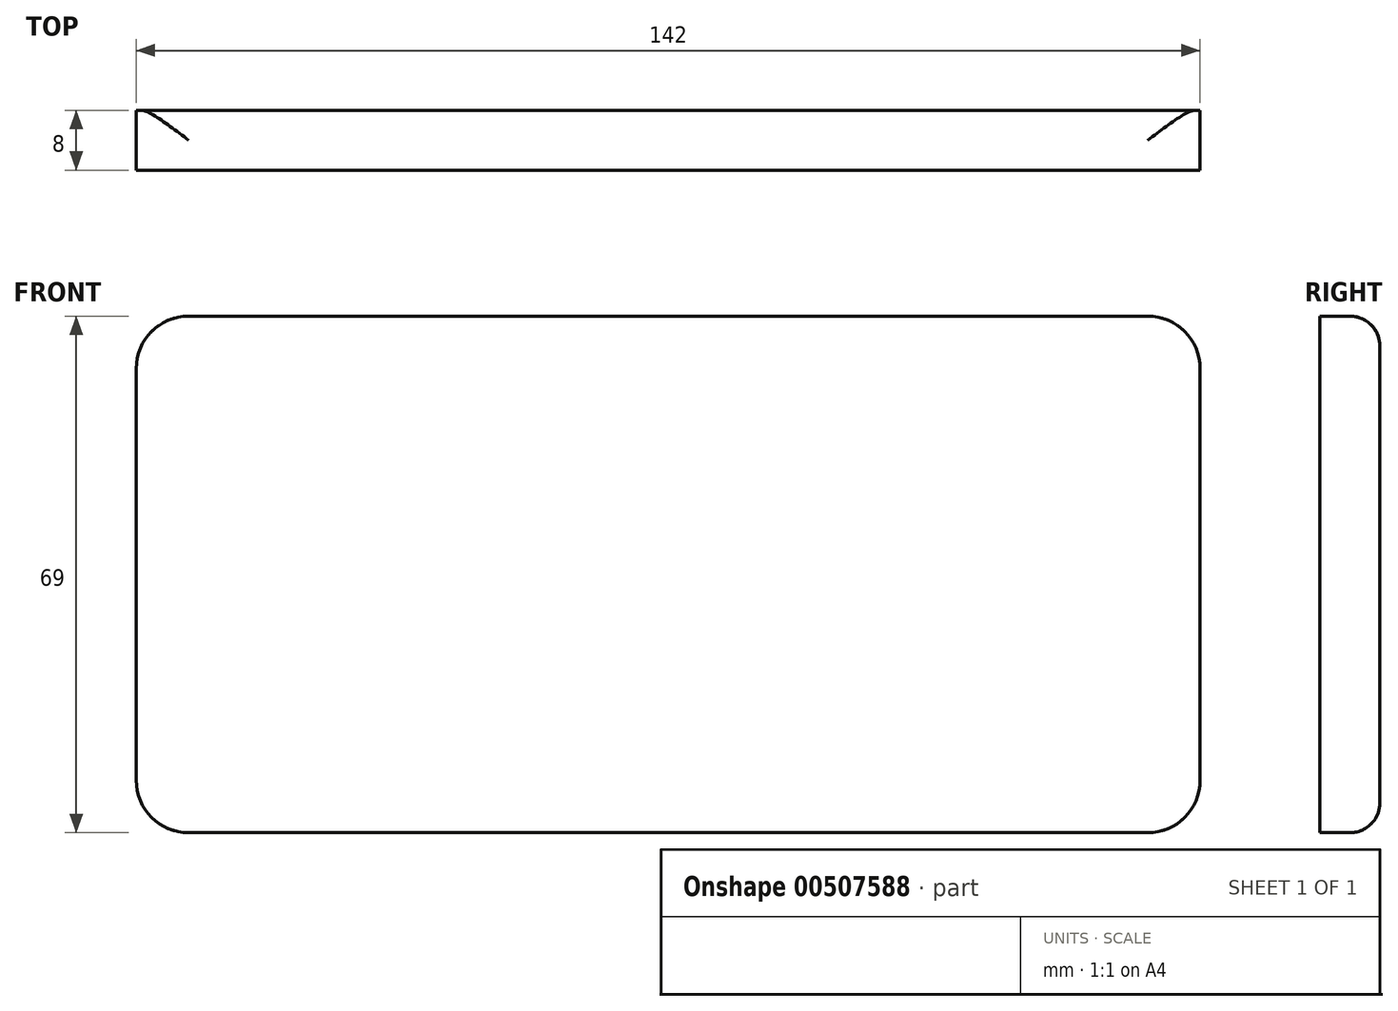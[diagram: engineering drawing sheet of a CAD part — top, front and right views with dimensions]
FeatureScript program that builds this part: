
annotation { "Feature Type Name" : "Feature", "Feature Type Description" : "" }
export const myFeature = defineFeature(function(context is Context, id is Id, definition is map)
    precondition{}
    {
        {
            var Q0;
            Q0=qCreatedBy(makeId("Front.planeOp"),FACE);
            var sketch = newSketch(context, id + "F0", { "sketchPlane" : qUnion([Q0])});
            skLineSegment(sketch, "E0.bottom", {"start": v(64, -34.5) * mm, "end": v(-64, -34.5) * mm});
            skLineSegment(sketch, "E0.top", {"start": v(64, 34.5) * mm, "end": v(-64, 34.5) * mm});
            skLineSegment(sketch, "E0.left", {"start": v(71, -27.5) * mm, "end": v(71, 27.5) * mm});
            skLineSegment(sketch, "E0.right", {"start": v(-71, -27.5) * mm, "end": v(-71, 27.5) * mm});
            skPoint(sketch, "E0.middle", {"position": v(0, 0) * mm});
            skPoint(sketch, "E1.visualSharp", {"position": v(71, 34.5) * mm});
            skArc(sketch, "E1.filletArc", {"start": v(71, 27.5) * mm, "mid": v(68.95, 32.45) * mm, "end": v(64, 34.5) * mm});
            skPoint(sketch, "E2.visualSharp", {"position": v(-71, 34.5) * mm});
            skArc(sketch, "E2.filletArc", {"start": v(-64, 34.5) * mm, "mid": v(-68.95, 32.45) * mm, "end": v(-71, 27.5) * mm});
            skPoint(sketch, "E3.visualSharp", {"position": v(-71, -34.5) * mm});
            skArc(sketch, "E3.filletArc", {"start": v(-71, -27.5) * mm, "mid": v(-68.95, -32.45) * mm, "end": v(-64, -34.5) * mm});
            skPoint(sketch, "E4.visualSharp", {"position": v(71, -34.5) * mm});
            skArc(sketch, "E4.filletArc", {"start": v(64, -34.5) * mm, "mid": v(68.95, -32.45) * mm, "end": v(71, -27.5) * mm});
            skSolve(sketch);
        }
        {
            var Q0;
            Q0 = qSketchRegion(id + "F0", true);
            extrude(context, id + "F1", {"entities" : qUnion([Q0]), "depth" : 4 * mm, "hasSecondDirection" : true, "secondDirectionOppositeDirection" : true, "secondDirectionDepth" : 4 * mm});
        }
        {
            var Q0;
            Q0=makeQuery(id+"F1.opExtrude","CAP_EDGE",EDGE,{"disambiguationData":[OSD([sQuery(id+"F0.wireOp",EDGE,"E0.top")])],"isStart":true});
            var Q1;
            Q1=makeQuery(id+"F1.opExtrude","CAP_EDGE",EDGE,{"disambiguationData":[OSD([sQuery(id+"F0.wireOp",EDGE,"E0.bottom")])],"isStart":true});
            fillet(context, id + "F2", {"entities" : qUnion([Q0, Q1]), "radius" : 4 * mm, "allowEdgeOverflow" : false});
        }
    });
